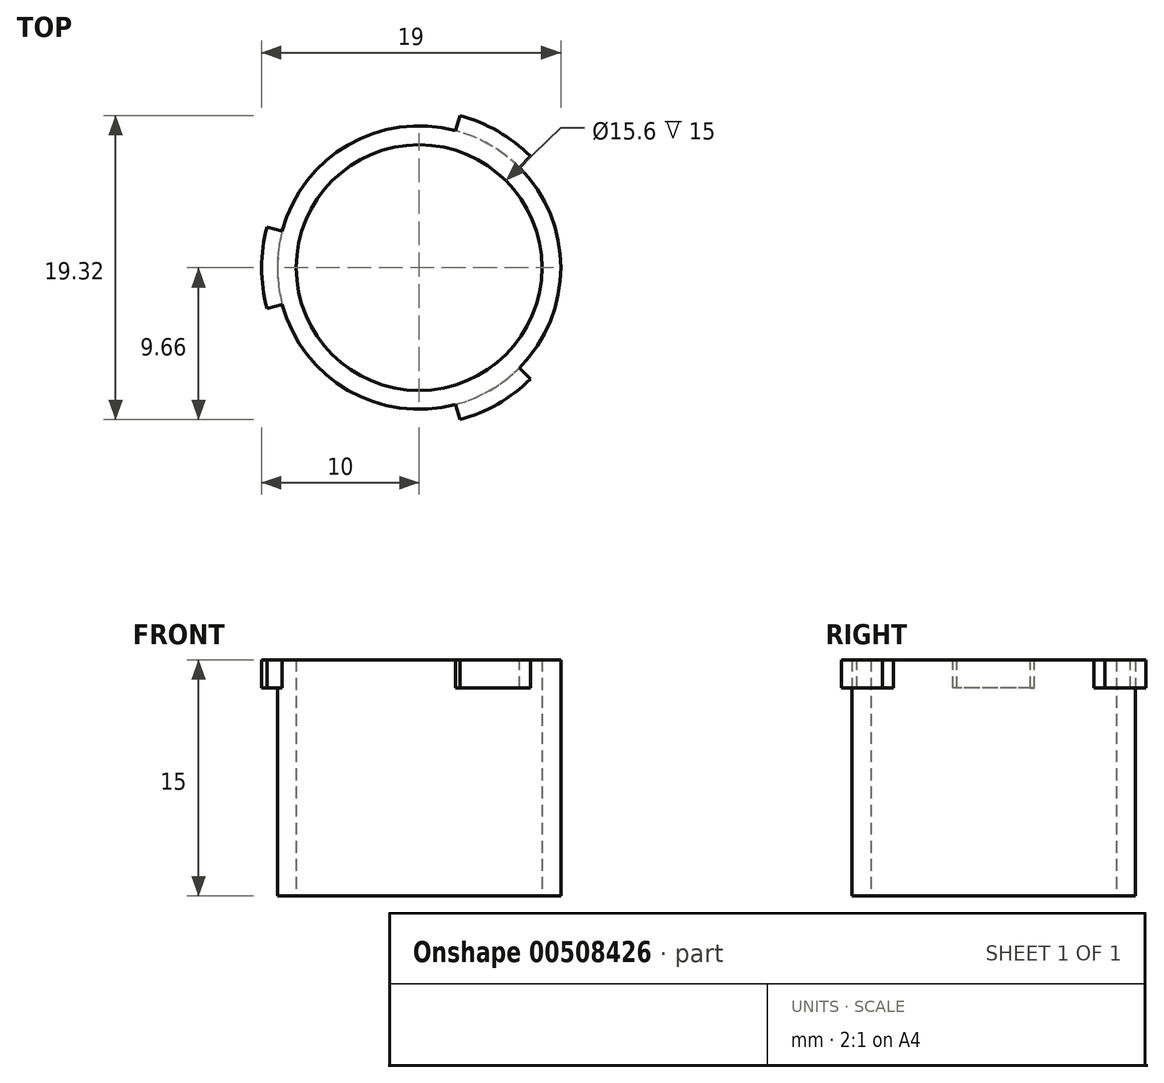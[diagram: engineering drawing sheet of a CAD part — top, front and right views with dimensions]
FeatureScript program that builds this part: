
annotation { "Feature Type Name" : "Feature", "Feature Type Description" : "" }
export const myFeature = defineFeature(function(context is Context, id is Id, definition is map)
    precondition{}
    {
        {
            var Q0;
            Q0=qCreatedBy(makeId("Top.planeOp"),FACE);
            var sketch = newSketch(context, id + "F0", { "sketchPlane" : qUnion([Q0])});
            skCircle(sketch, "E0", {"center": v(0, 0) * mm, "radius": 9 * mm});
            skSolve(sketch);
        }
        {
            var Q0;
            Q0=makeQuery(id+"F0.imprint","IMPRINT",FACE,{"disambiguationData":[TD([[makeQuery(id+"F0.imprint","IMPRINT",EDGE,{"derivedFrom":sQuery(id+"F0.wireOp",EDGE,"E0")}),1.0]])]});
            extrude(context, id + "F1", {"entities" : qUnion([Q0]), "depth" : 15 * mm});
        }
        {
            var Q0;
            Q0=makeQuery(id+"F1.opExtrude","CAP_FACE",FACE,{"disambiguationData":[OSD([sQuery(id+"F0.wireOp",EDGE,"E0")])],"isStart":false});
            var sketch = newSketch(context, id + "F2", { "sketchPlane" : qUnion([Q0])});
            skCircle(sketch, "E1", {"center": v(0, 0) * mm, "radius": 10 * mm});
            skLineSegment(sketch, "E2", {"start": v(-10, 0) * mm, "end": v(-12.77, 0) * mm});
            skLineSegment(sketch, "E3", {"start": v(5, 8.66) * mm, "end": v(6.7, 11.62) * mm});
            skLineSegment(sketch, "E4", {"start": v(5, -8.66) * mm, "end": v(7.54, -13.06) * mm});
            skLineSegment(sketch, "E5", {"start": v(6.36, -6.36) * mm, "end": v(7.07, -7.07) * mm});
            skLineSegment(sketch, "E6", {"start": v(2.33, -8.7) * mm, "end": v(2.59, -9.66) * mm});
            skLineSegment(sketch, "E7", {"start": v(-8.7, 2.33) * mm, "end": v(-9.66, 2.59) * mm});
            skLineSegment(sketch, "E8", {"start": v(2.33, 8.7) * mm, "end": v(2.59, 9.66) * mm});
            skLineSegment(sketch, "E9", {"start": v(6.36, 6.36) * mm, "end": v(7.07, 7.07) * mm});
            skLineSegment(sketch, "E10", {"start": v(-8.7, -2.33) * mm, "end": v(-9.66, -2.59) * mm});
            skCircle(sketch, "E11", {"center": v(0, 0) * mm, "radius": 9 * mm});
            skSolve(sketch);
        }
        {
            var Q0;
            {var subQ1=sQuery(id+"F2.wireOp",EDGE,"E8");Q0=makeQuery(id+"F2.imprint","IMPRINT",FACE,{"disambiguationData":[TD([[makeQuery(id+"F2.imprint","IMPRINT",EDGE,{"derivedFrom":subQ1}),-1.0]])]});}
            var Q1;
            {var subQ1=sQuery(id+"F2.wireOp",EDGE,"E5");Q1=makeQuery(id+"F2.imprint","IMPRINT",FACE,{"disambiguationData":[TD([[makeQuery(id+"F2.imprint","IMPRINT",EDGE,{"derivedFrom":subQ1}),-1.0]])]});}
            var Q2;
            {var subQ0=sQuery(id+"F2.wireOp",EDGE,"E7");Q2=makeQuery(id+"F2.imprint","IMPRINT",FACE,{"disambiguationData":[TD([[makeQuery(id+"F2.imprint","IMPRINT",EDGE,{"derivedFrom":subQ0}),1.0]])]});}
            extrude(context, id + "F3", {"entities" : qUnion([Q0, Q1, Q2]), "operationType" : NewBodyOperationType.ADD, "oppositeDirection" : true, "depth" : 1.8 * mm});
        }
        {
            var Q0;
            Q0=makeQuery(id+"F1.opExtrude","CAP_FACE",FACE,{"disambiguationData":[OSD([sQuery(id+"F0.wireOp",EDGE,"E0")])],"isStart":true});
            var sketch = newSketch(context, id + "F4", { "sketchPlane" : qUnion([Q0])});
            skCircle(sketch, "E12", {"center": v(0, 0) * mm, "radius": 7.8 * mm});
            skSolve(sketch);
        }
        {
            var Q0;
            Q0=makeQuery(id+"F4.imprint","IMPRINT",FACE,{"disambiguationData":[TD([[makeQuery(id+"F4.imprint","IMPRINT",EDGE,{"derivedFrom":sQuery(id+"F4.wireOp",EDGE,"E12")}),1.0]])]});
            extrude(context, id + "F5", {"entities" : qUnion([Q0]), "operationType" : NewBodyOperationType.REMOVE, "oppositeDirection" : true, "depth" : 25 * mm});
        }
    });
